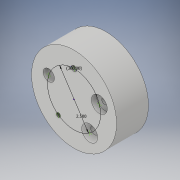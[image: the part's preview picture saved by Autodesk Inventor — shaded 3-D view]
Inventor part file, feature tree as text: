
AUTODESK INVENTOR PART (.ipt)
format: ipt  version: 2017 (Build 210142000, 142)  size: 126,976 bytes
history: native  units: in
note: dims shown in document units (in); Inventor stores cm internally (conversion verified against a paired STEP export)
features: hole x5, sketch x2, extrude x1
ambient origin geometry x8: Origin, YZ Plane, XZ Plane, XY Plane, X Axis, Y Axis, Z Axis, Center Point
bodies: Solid1 (feature_tree)
feature tree (8):
  extrude  "Extrusion1"  Depth=1.5in
  sketch  "Sketch2"  dims[d9=1.9685in d11=360.0deg d13=0.25in d14=0.75in d15=0.375in d16=0.25in d17=0.5635in d18=1.5in d19=0.8108in d20=0.275in d21=0.75in d22=0.75in d23=0.25in d24=0.5635in d25=1.5in d26=0.8108in d27=0.357in d28=0.75in d29=0.75in d30=0.25in d31=0.5635in d32=1.5in d33=0.8108in d34=0.196in d35=0.5in d36=0.75in d37=0.25in d38=0.5635in d39=0.75in d40=0.8108in d41=0.531in d42=0.5in d43=1.125in d44=0.364in d45=0.5635in d46=0.75in d47=0.8108in]
  hole  "Hole1"  [1 undecoded]
  hole  "Hole2"  [1 undecoded]
  hole  "Hole3"  [1 undecoded]
  hole  "Hole4"  [1 undecoded]
  hole  "Hole5"  [1 undecoded]
  sketch  "Sketch1"  dims[d6=1.5in d7=0.0in d8=2.5in]
note: 5 required parameter values undecoded (feature->parameter linkage not recoverable at this tier; creation-order binding heuristic only, values carry confidence <= 0.55)
